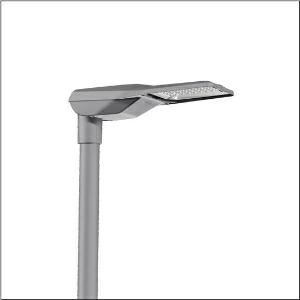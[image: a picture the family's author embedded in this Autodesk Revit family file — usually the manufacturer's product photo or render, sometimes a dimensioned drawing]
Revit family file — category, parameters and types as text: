
# Revit family: streetlight_sl_21_iq_mini___p1_0a_5xe2a31d08hb_09ea
name_source: partatom
category: Lighting Fixtures
units: mm (PartAtom-declared; Revit-internal decimal feet)

## family parameters
Cut with Voids When Loaded = No
Host = Face
Light Source = No
Part Type = Normal
Room Calculation Point = No
Round Connector Dimension = Use Diameter
Shared = No

## types (1)
- --- (1 x LED, 9450 lm, 70.9 W, 3000K)
    Apparent Load = 71 VA
    CIE Flux Codes = 21 50 90 100 100
    Color Rendering = 70
    Color Temperature = 3000K
    Default Elevation = 1800 mm
    Description = Streetlight SL 21 iQ mini, mast luminaire, primary light control with lens, of PMMA, primary optical cover: cover, of toughened safety glass, transparent, light distribution: P1.0a, light emission: direct distribution, primary light characteristic: asymmetric, installation type: post-top, side-entry, LED, High Power LED, rated luminous flux: 9.450lm, luminous efficacy: 133lm/W, light colour: 730, colour temperature: 3000K, control: Auto-Match, Temp-Guard, Lumen-Switch, Night-Set, Smart-Wire, Light-Fading, Desk-Remote (wireless, voltage-free reading and setting of iQ features in the workshop via application-optimized NFC function/RFID function), optimised constant luminous flux control (CLO 2.0), presetting dimming linear, mains connection: 220..240V, AC, 50/60Hz, start of lifetime: 71W, end of service life: 75W, reduction: 31W, luminaire housing, of diecast aluminium, powder-coated, Siteco® metallic grey (DB 702S), corrosivity category C5 mid according to DIN EN ISO 12944, please order mast flange separately, inclination adjustable: 0°, 5°, 10°, 15°, sealing non-destructively replaceable, multi-level sealing system, length: 628mm, width: 235mm, height: 110mm, mast flange for spigot size: 42mm (side-entry): 5XC10008XM4, 60/48mm (side-entry/post-top): 5XC10108XM2, 76/60mm (side-entry/post-top): 5XC10108XM1, protection rating (complete): IP66, insulation class (complete): insulation class II (safety insulation), certification: CE, ENEC, ENEC+, VDE, impact resistance: IK09, permissible operating ambient temperature for outdoor applications: -40..+50°C, standard-compliant lighting for roads and squares, packaging unit: 1 piece

Light Distribution: P1.0a
    Height = 110 mm
    Lamp = 1 x LED
    Lamp Light Flux = 9450 lm
    Lamp Power = 70.9 W
    Lamp count = 1
    Length = 625 mm
    Luminous efficacy = 133 lm/W
    Manufacturer = Siteco
    ModVariant = No
    Model = 5XE2A31D08HB
    Number of Poles = 1
    OnlyDefault = Yes
    Power Factor = 1
    Product Name = Streetlight SL 21 iQ mini | P1.0a
    Product group = mast luminaire | pylon top
    ProductGroupID = 6100
    Protection Class = Protection class II
    Protection Degree = IP 66
    RLX_Detail_Level = 1
    RLX_Emergency_Light_Flux = 0 lm
    RLX_Emergency_Type = 0
    RLX_Emergency_Type_DB = No
    RlxData = <blob elided: 103565 chars, md5=d8a45c82>
    Socket = socket
    Standby Power = 0 W
    System Light Flux = 9450 lm
    System Power = 71 W
    Type Comments = factory setting: luminous flux: 100 % | dim-lin: 254 | 711 mA
    Type Image = l_1003519.jpg
    URL = http://relux.com
    VarID = @adj_107891
    Voltage = 0 V
    Weight = 0.00 kg
    Width = 234 mm

## geometry (parser evidence)
native form markers: Blend x4, Sweep x8
no freeform markers — native parametric forms only
